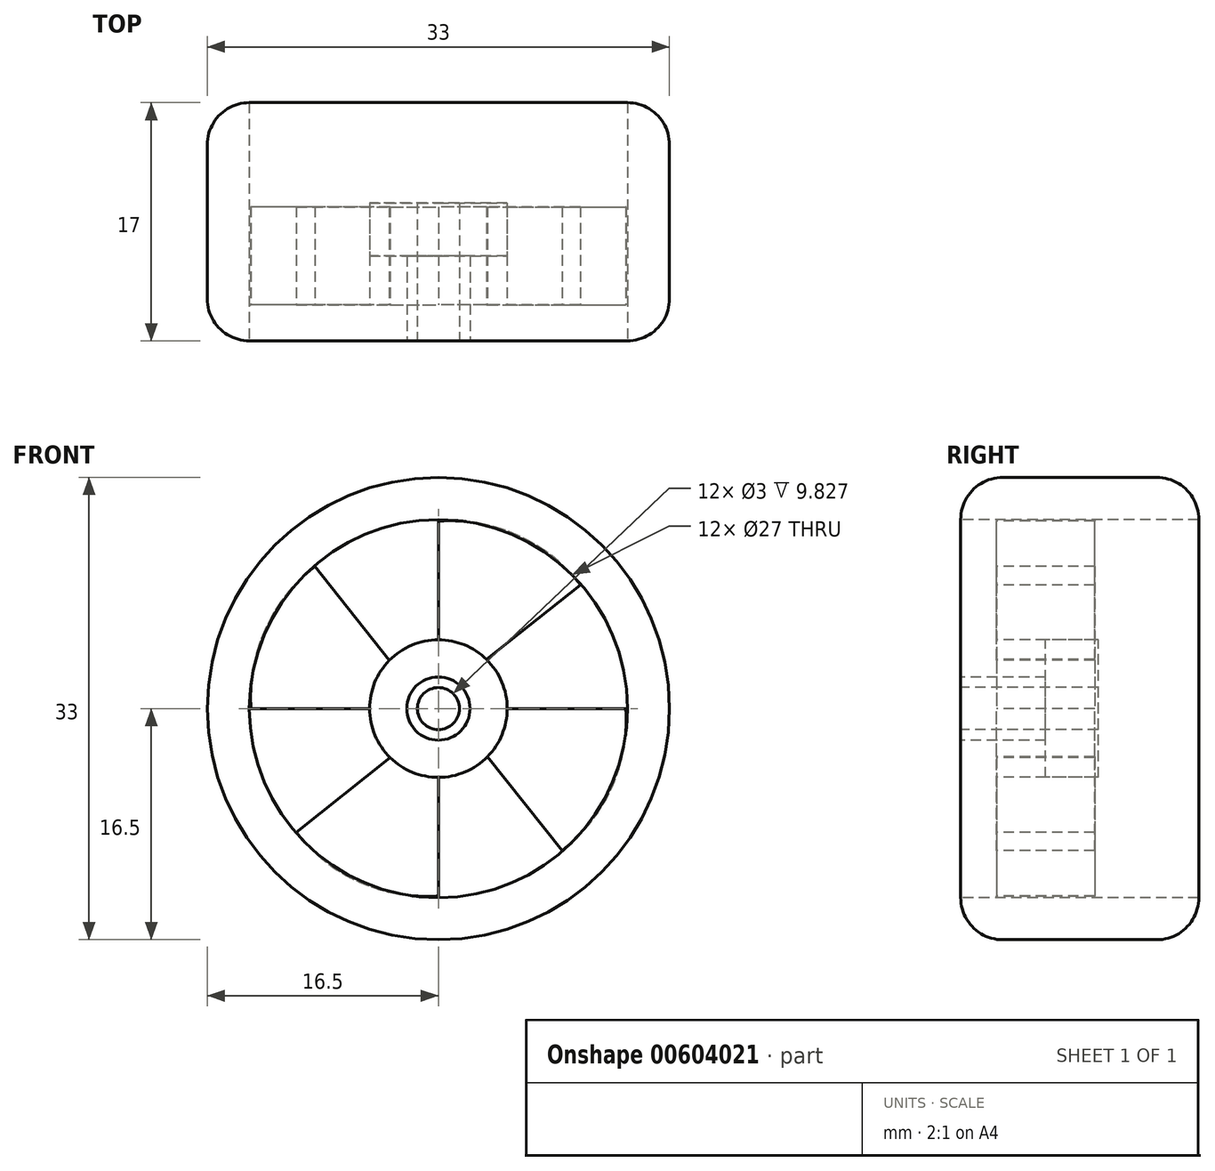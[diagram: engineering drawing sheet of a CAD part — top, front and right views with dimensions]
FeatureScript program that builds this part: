
annotation { "Feature Type Name" : "Feature", "Feature Type Description" : "" }
export const myFeature = defineFeature(function(context is Context, id is Id, definition is map)
    precondition{}
    {
        {
            var Q0;
            Q0=qCreatedBy(makeId("Right.planeOp"),FACE);
            var sketch = newSketch(context, id + "F0", { "sketchPlane" : qUnion([Q0])});
            skLineSegment(sketch, "E0.top", {"start": v(0, 16.5) * mm, "end": v(17, 16.5) * mm});
            skLineSegment(sketch, "E0.left", {"start": v(0, 0) * mm, "end": v(0, 2.26) * mm});
            skLineSegment(sketch, "E0.right", {"start": v(17, 13.5) * mm, "end": v(17, 16.5) * mm});
            skLineSegment(sketch, "E1", {"start": v(17, 13.5) * mm, "end": v(0, 13.5) * mm});
            skLineSegment(sketch, "E2", {"start": v(0, 2.26) * mm, "end": v(6.06, 2.26) * mm});
            skLineSegment(sketch, "E3", {"start": v(6.06, 2.26) * mm, "end": v(6.06, 4.91) * mm});
            skLineSegment(sketch, "E4", {"start": v(6.06, 4.91) * mm, "end": v(9.83, 4.91) * mm});
            skLineSegment(sketch, "E5", {"start": v(9.83, 1.5) * mm, "end": v(9.83, 4.91) * mm});
            skLineSegment(sketch, "E6", {"start": v(9.83, 1.5) * mm, "end": v(0, 1.5) * mm});
            skLineSegment(sketch, "E7.trimOffspring", {"start": v(0, 13.5) * mm, "end": v(0, 16.5) * mm});
            skLineSegment(sketch, "E8", {"start": v(-20.75, 0) * mm, "end": v(30.46, 0) * mm, "construction": true});
            skSolve(sketch);
        }
        {
            var Q0;
            Q0 = qSketchRegion(id + "F0", true);
            var Q1;
            Q1=sQuery(id+"F0.wireOp",EDGE,"E8");
            revolve(context, id + "F1", {"entities" : qUnion([Q0]), "axis" : qUnion([Q1]), "revolveType" : RevolveType.FULL});
        }
        {
            var Q0;
            Q0=makeQuery(id+"F1.opRevolve","SWEPT_FACE",FACE,{"disambiguationData":[OSD([sQuery(id+"F0.wireOp",EDGE,"E3")])]});
            var sketch = newSketch(context, id + "F2", { "sketchPlane" : qUnion([Q0])});
            skLineSegment(sketch, "E9", {"start": v(0, 4.91) * mm, "end": v(0, 13.38) * mm});
            skLineSegment(sketch, "E10", {"start": v(3.44, 3.5) * mm, "end": v(10.14, 8.83) * mm});
            skArc(sketch, "E11", {"start": v(10.14, 8.83) * mm, "mid": v(5.64, 12.38) * mm, "end": v(0, 13.38) * mm});
            skArc(sketch, "E12", {"start": v(3.44, 3.5) * mm, "mid": v(1.84, 4.52) * mm, "end": v(0, 4.91) * mm});
            skSolve(sketch);
        }
        {
            var Q0;
            {var subQ0=sQuery(id+"F2.wireOp",EDGE,"E9");Q0=makeQuery(id+"F2.imprint","IMPRINT",FACE,{"disambiguationData":[TD([[makeQuery(id+"F2.imprint","IMPRINT",EDGE,{"derivedFrom":subQ0}),-1.0]])]});}
            extrude(context, id + "F3", {"entities" : qUnion([Q0]), "endBound" : BoundingType.SYMMETRIC, "oppositeDirection" : true, "depth" : 7 * mm, "offsetDistance" : 25 * mm});
        }
        {
            var Q0;
            Q0=makeQuery(id+"F3.opExtrude","SWEPT_BODY",BODY,{"disambiguationData":[OSD([sQuery(id+"F0.wireOp",EDGE,"E3"),sQuery(id+"F0.wireOp",EDGE,"E4"),sQuery(id+"F2.wireOp",EDGE,"E9"),sQuery(id+"F2.wireOp",EDGE,"E10"),sQuery(id+"F2.wireOp",EDGE,"E11")])]});
            var Q1;
            Q1=makeQuery(id+"F1.opRevolve","SWEPT_EDGE",EDGE,{"disambiguationData":[OSD([sQuery(id+"F0.wireOp",EDGE,"E4"),sQuery(id+"F0.wireOp",EDGE,"E5")])]});
            circularPattern(context, id + "F4", {"entities" : qUnion([Q0]), "axis" : qUnion([Q1]), "angle" : 360 * degree, "instanceCount" : 4, "equalSpace" : true});
        }
        {
            var Q0;
            Q0=makeQuery(id+"F1.opRevolve","SWEPT_EDGE",EDGE,{"disambiguationData":[OSD([sQuery(id+"F0.wireOp",EDGE,"E0.top"),sQuery(id+"F0.wireOp",EDGE,"E7.trimOffspring")])]});
            var Q1;
            Q1=makeQuery(id+"F1.opRevolve","SWEPT_EDGE",EDGE,{"disambiguationData":[OSD([sQuery(id+"F0.wireOp",EDGE,"E0.top"),sQuery(id+"F0.wireOp",EDGE,"E0.right")])]});
            fillet(context, id + "F5", {"entities" : qUnion([Q0, Q1]), "radius" : 3 * mm, "tangentPropagation" : true, "allowEdgeOverflow" : false});
        }
    });
